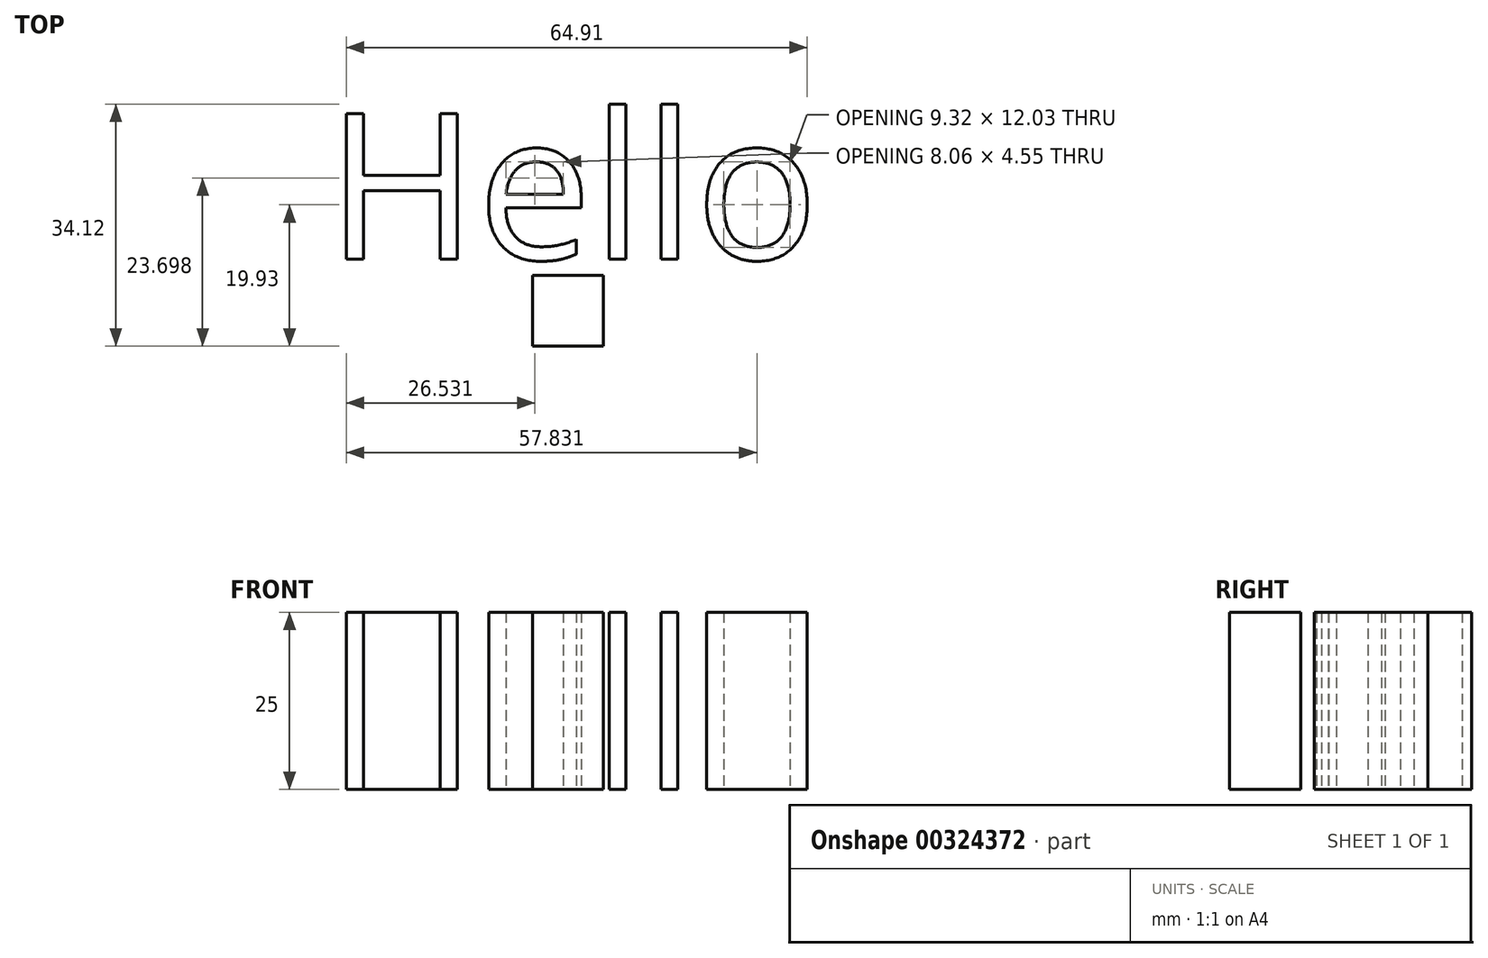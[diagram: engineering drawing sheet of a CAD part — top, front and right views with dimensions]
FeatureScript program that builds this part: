
annotation { "Feature Type Name" : "Feature", "Feature Type Description" : "" }
export const myFeature = defineFeature(function(context is Context, id is Id, definition is map)
    precondition{}
    {
        {
            var Q0;
            Q0=qCreatedBy(makeId("Top.planeOp"),FACE);
            var sketch = newSketch(context, id + "F0", { "sketchPlane" : qUnion([Q0])});
            skLineSegment(sketch, "E0.bottom", {"start": v(0, 0) * mm, "end": v(10, 0) * mm});
            skLineSegment(sketch, "E0.top", {"start": v(0, 10) * mm, "end": v(10, 10) * mm});
            skLineSegment(sketch, "E0.left", {"start": v(0, 0) * mm, "end": v(0, 10) * mm});
            skLineSegment(sketch, "E0.right", {"start": v(10, 0) * mm, "end": v(10, 10) * mm});
            skText(sketch, "E1", { "text": "Hello", "fontName": "OpenSans-Regular.ttf"});
            const initialGuessF0  = {"E1": [-0.02905, 0.01224, 1, 0, 0.02073]};
            skSetInitialGuess(sketch, initialGuessF0);
            skSolve(sketch);
        }
        {
            var Q0;
            Q0 = qSketchRegion(id + "F0", true);
            extrude(context, id + "F1", {"entities" : qUnion([Q0]), "depth" : 25 * mm});
        }
    });
